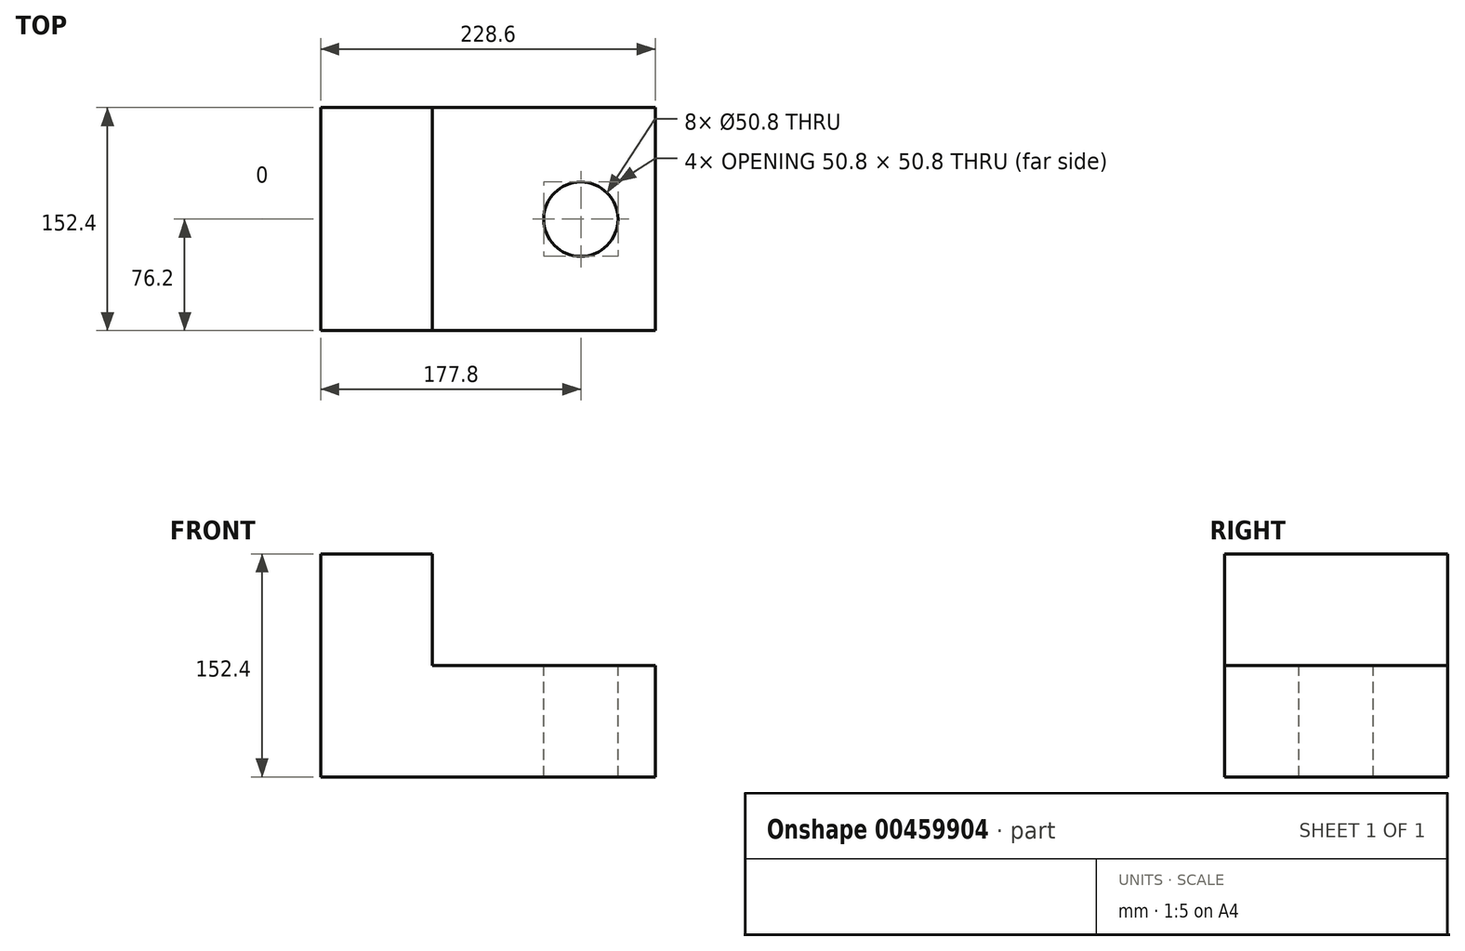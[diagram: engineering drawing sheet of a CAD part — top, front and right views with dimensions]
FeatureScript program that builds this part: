
annotation { "Feature Type Name" : "Feature", "Feature Type Description" : "" }
export const myFeature = defineFeature(function(context is Context, id is Id, definition is map)
    precondition{}
    {
        {
            var Q0;
            Q0=qCreatedBy(makeId("Front.planeOp"),FACE);
            var sketch = newSketch(context, id + "F0", { "sketchPlane" : qUnion([Q0])});
            skLineSegment(sketch, "E0", {"start": v(0, 0) * mm, "end": v(-228.6, 0) * mm});
            skLineSegment(sketch, "E1", {"start": v(-228.6, 0) * mm, "end": v(-228.6, 152.4) * mm});
            skLineSegment(sketch, "E2", {"start": v(-228.6, 152.4) * mm, "end": v(-152.4, 152.4) * mm});
            skLineSegment(sketch, "E3", {"start": v(-152.4, 152.4) * mm, "end": v(-152.4, 76.2) * mm});
            skLineSegment(sketch, "E4", {"start": v(-152.4, 76.2) * mm, "end": v(0, 76.2) * mm});
            skLineSegment(sketch, "E5", {"start": v(0, 76.2) * mm, "end": v(0, 0) * mm});
            skSolve(sketch);
        }
        {
            var Q0;
            Q0=makeQuery(id+"F0.imprint","IMPRINT",FACE,{"disambiguationData":[TD([[makeQuery(id+"F0.imprint","IMPRINT",EDGE,{"derivedFrom":sQuery(id+"F0.wireOp",EDGE,"E0")}),-1.0]])]});
            extrude(context, id + "F1", {"entities" : qUnion([Q0]), "depth" : 152.4 * mm});
        }
        {
            var Q0;
            Q0=makeQuery(id+"F1.opExtrude","SWEPT_FACE",FACE,{"disambiguationData":[OSD([sQuery(id+"F0.wireOp",EDGE,"E4")])]});
            var sketch = newSketch(context, id + "F2", { "sketchPlane" : qUnion([Q0])});
            skPoint(sketch, "E6", {"position": v(-50.8, -76.2) * mm});
            skCircle(sketch, "E7", {"center": v(-50.8, -76.2) * mm, "radius": 25.4 * mm});
            skSolve(sketch);
        }
        {
            var Q0;
            Q0=sQuery(id+"F2.wireOp",VERTEX,"E6");
            var Q1;
            Q1=makeQuery(id+"F1.opExtrude","SWEPT_BODY",BODY,{"disambiguationData":[OSD([sQuery(id+"F0.wireOp",EDGE,"E0"),sQuery(id+"F0.wireOp",EDGE,"E1"),sQuery(id+"F0.wireOp",EDGE,"E2"),sQuery(id+"F0.wireOp",EDGE,"E3"),sQuery(id+"F0.wireOp",EDGE,"E4"),sQuery(id+"F0.wireOp",EDGE,"E5")])]});
            hole(context, id + "F3", {"style" : HoleStyle.SIMPLE, "endStyle" : HoleEndStyle.THROUGH, "holeDiameter" : 50.8 * mm, "isTappedThrough" : true, "tappedDepth" : 12.7 * mm, "tapClearance" : 3, "locations" : qUnion([Q0]), "scope" : qUnion([Q1])});
        }
    });
